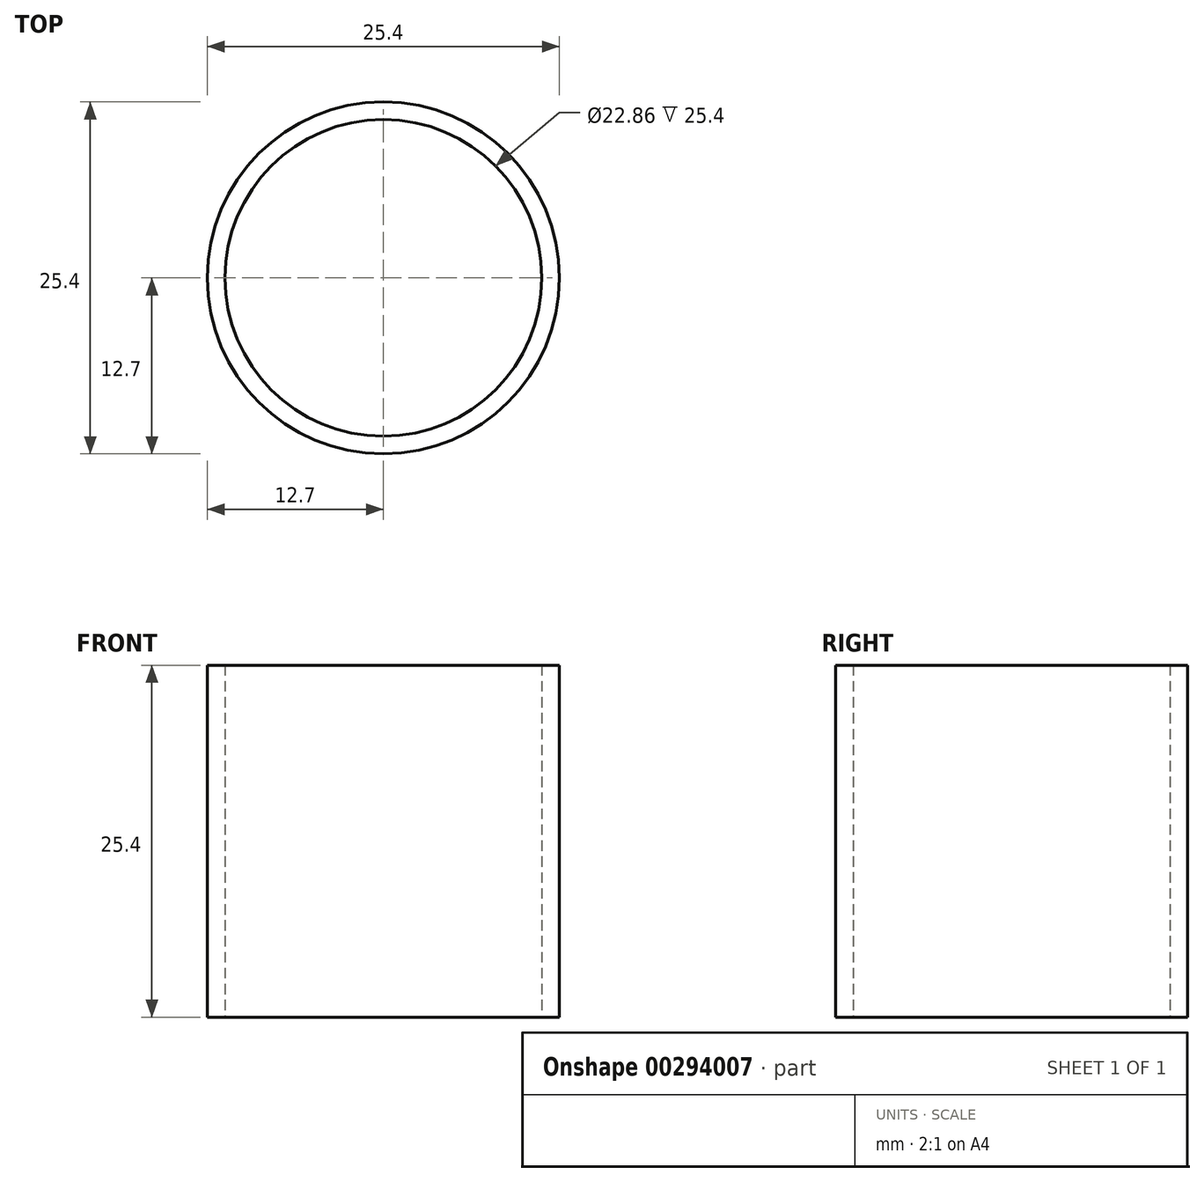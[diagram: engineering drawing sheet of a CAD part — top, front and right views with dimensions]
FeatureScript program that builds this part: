
annotation { "Feature Type Name" : "Feature", "Feature Type Description" : "" }
export const myFeature = defineFeature(function(context is Context, id is Id, definition is map)
    precondition{}
    {
        {
            var Q0;
            Q0=qCreatedBy(makeId("Top.planeOp"),FACE);
            var sketch = newSketch(context, id + "F0", { "sketchPlane" : qUnion([Q0])});
            skCircle(sketch, "E0", {"center": v(0, 0) * mm, "radius": 12.7 * mm});
            skCircle(sketch, "E1", {"center": v(0, 0) * mm, "radius": 11.43 * mm});
            skSolve(sketch);
        }
        {
            var Q0;
            Q0=makeQuery(id+"F0.imprint","IMPRINT",FACE,{"disambiguationData":[TD([[makeQuery(id+"F0.imprint","IMPRINT",EDGE,{"derivedFrom":sQuery(id+"F0.wireOp",EDGE,"E0")}),1.0]])]});
            extrude(context, id + "F1", {"entities" : qUnion([Q0]), "depth" : 25.4 * mm});
        }
    });
